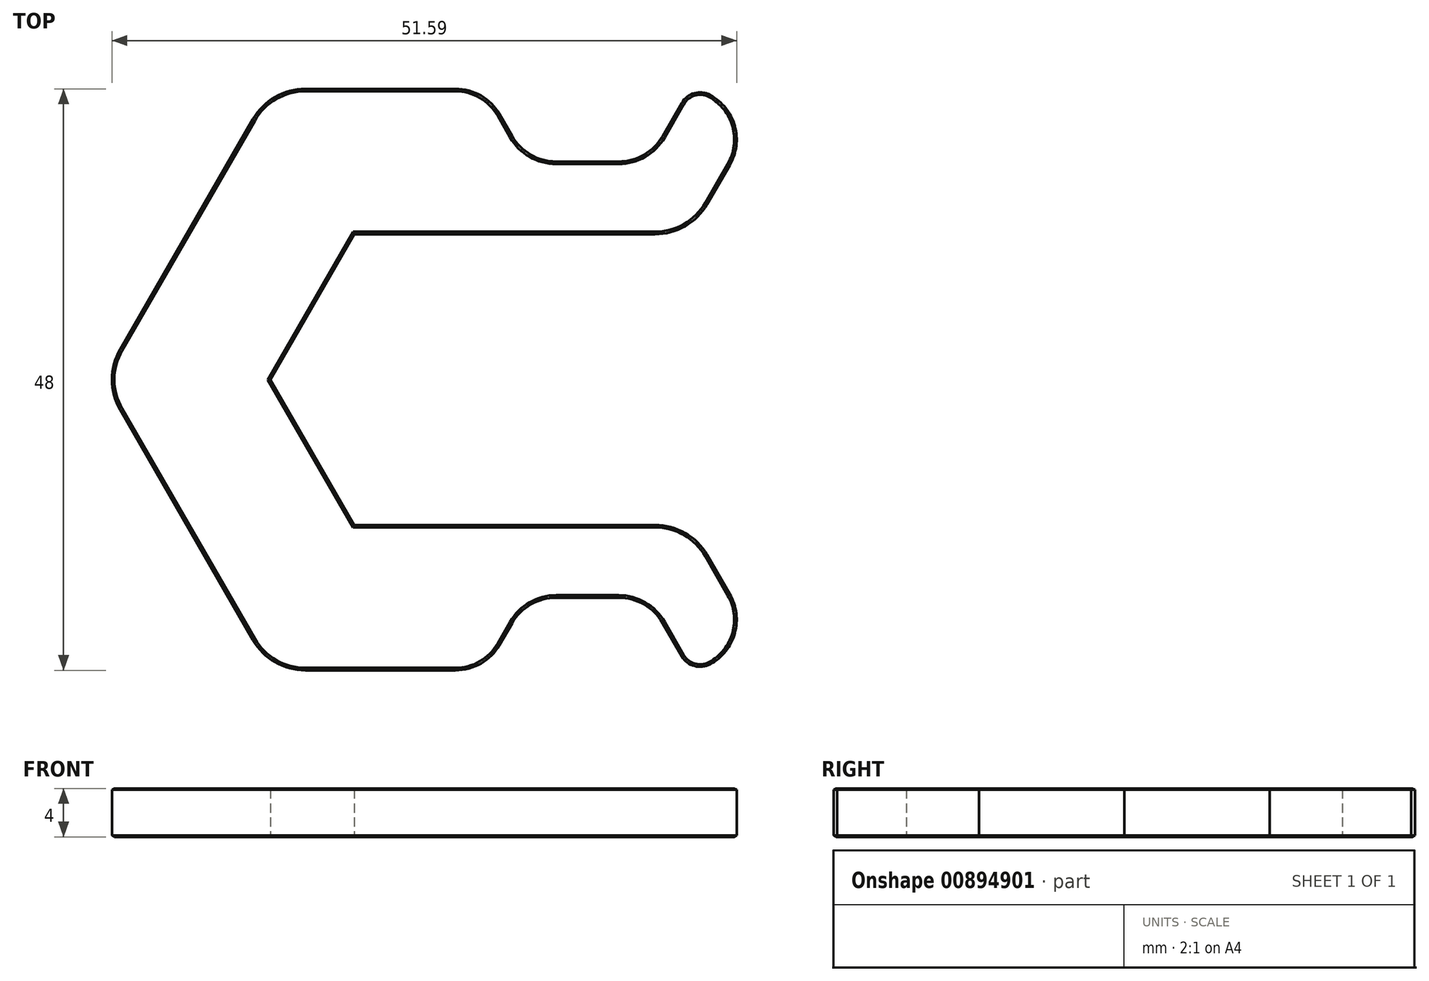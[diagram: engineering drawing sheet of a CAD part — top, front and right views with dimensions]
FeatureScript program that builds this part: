
annotation { "Feature Type Name" : "Feature", "Feature Type Description" : "" }
export const myFeature = defineFeature(function(context is Context, id is Id, definition is map)
    precondition{}
    {
        {
            var Q0;
            Q0=qCreatedBy(makeId("Top.planeOp"),FACE);
            var sketch = newSketch(context, id + "F0", { "sketchPlane" : qUnion([Q0])});
            skCircle(sketch, "E0.cCircle", {"center": v(0, 0) * mm, "radius": 12 * mm, "construction": true});
            skLineSegment(sketch, "E0.0", {"start": v(6.93, -12) * mm, "end": v(-6.93, -12) * mm});
            skLineSegment(sketch, "E0.1", {"start": v(-6.93, -12) * mm, "end": v(-13.86, 0) * mm});
            skLineSegment(sketch, "E0.2", {"start": v(-13.86, 0) * mm, "end": v(-6.93, 12) * mm});
            skLineSegment(sketch, "E0.3", {"start": v(-6.93, 12) * mm, "end": v(6.93, 12) * mm});
            skLineSegment(sketch, "E0.4", {"start": v(6.93, 12) * mm, "end": v(13.86, 0) * mm, "construction": true});
            skLineSegment(sketch, "E0.5", {"start": v(13.86, 0) * mm, "end": v(6.93, -12) * mm, "construction": true});
            skPoint(sketch, "E0.0.midPoint", {"position": v(0, -12) * mm});
            skCircle(sketch, "E1.cCircle", {"center": v(0, 0) * mm, "radius": 24 * mm, "construction": true});
            skLineSegment(sketch, "E1.0", {"start": v(13.86, -24) * mm, "end": v(-13.86, -24) * mm});
            skLineSegment(sketch, "E1.1", {"start": v(-13.86, -24) * mm, "end": v(-27.71, 0) * mm});
            skLineSegment(sketch, "E1.2", {"start": v(-27.71, 0) * mm, "end": v(-13.86, 24) * mm});
            skLineSegment(sketch, "E1.3", {"start": v(-13.86, 24) * mm, "end": v(13.86, 24) * mm});
            skLineSegment(sketch, "E1.4", {"start": v(13.86, 24) * mm, "end": v(27.71, 0) * mm});
            skLineSegment(sketch, "E1.5", {"start": v(27.71, 0) * mm, "end": v(13.86, -24) * mm});
            skPoint(sketch, "E1.0.midPoint", {"position": v(0, -24) * mm});
            skLineSegment(sketch, "E2", {"start": v(6.93, 12) * mm, "end": v(13.86, 24) * mm});
            skLineSegment(sketch, "E3", {"start": v(6.93, -12) * mm, "end": v(20.78, -12) * mm});
            skLineSegment(sketch, "E4", {"start": v(20.78, -12) * mm, "end": v(27.71, -24) * mm});
            skLineSegment(sketch, "E5", {"start": v(27.71, -24) * mm, "end": v(13.86, -24) * mm});
            skLineSegment(sketch, "E6", {"start": v(20.78, -24) * mm, "end": v(17.32, -18) * mm});
            skLineSegment(sketch, "E7", {"start": v(7.32, -18) * mm, "end": v(3.86, -24) * mm});
            skLineSegment(sketch, "E8", {"start": v(17.32, -18) * mm, "end": v(7.32, -18) * mm});
            skLineSegment(sketch, "E9", {"start": v(-13.86, 0) * mm, "end": v(-27.71, 0) * mm});
            skSolve(sketch);
        }
        {
            var Q0;
            Q0=makeQuery(id+"F0.imprint","IMPRINT",FACE,{"disambiguationData":[TD([[makeQuery(id+"F0.imprint","IMPRINT",EDGE,{"derivedFrom":sQuery(id+"F0.wireOp",EDGE,"E0.0")}),1.0]])]});
            var Q1;
            {var subQ2=sQuery(id+"F0.wireOp",EDGE,"E4");Q1=makeQuery(id+"F0.imprint","IMPRINT",FACE,{"disambiguationData":[TD([[makeQuery(id+"F0.imprint","IMPRINT",EDGE,{"derivedFrom":subQ2}),-1.0]])]});}
            extrude(context, id + "F1", {"entities" : qUnion([Q0, Q1]), "depth" : 4 * mm, "offsetDistance" : 25 * mm});
        }
        {
            var Q0;
            Q0=makeQuery(id+"F1.opExtrude","SWEPT_EDGE",EDGE,{"disambiguationData":[OSD([sQuery(id+"F0.wireOp",EDGE,"E1.0"),sQuery(id+"F0.wireOp",EDGE,"E1.1")])]});
            var Q1;
            Q1=makeQuery(id+"F1.opExtrude","SWEPT_EDGE",EDGE,{"disambiguationData":[OSD([sQuery(id+"F0.wireOp",EDGE,"E1.3"),sQuery(id+"F0.wireOp",EDGE,"E1.4"),sQuery(id+"F0.wireOp",EDGE,"E2")])]});
            var Q2;
            Q2=makeQuery(id+"F1.opExtrude","SWEPT_EDGE",EDGE,{"disambiguationData":[OSD([sQuery(id+"F0.wireOp",EDGE,"E1.5"),sQuery(id+"F0.wireOp",EDGE,"E3")])]});
            fillet(context, id + "F2", {"entities" : qUnion([Q0, Q1, Q2]), "radius" : 5 * mm, "tangentPropagation" : true, "allowEdgeOverflow" : false});
        }
        {
            var Q0;
            Q0=makeQuery(id+"F1.opExtrude","SWEPT_EDGE",EDGE,{"disambiguationData":[OSD([sQuery(id+"F0.wireOp",EDGE,"E1.0"),sQuery(id+"F0.wireOp",EDGE,"E7")])]});
            var Q1;
            Q1=makeQuery(id+"F1.opExtrude","SWEPT_EDGE",EDGE,{"disambiguationData":[OSD([sQuery(id+"F0.wireOp",EDGE,"E7"),sQuery(id+"F0.wireOp",EDGE,"E8")])]});
            var Q2;
            Q2=makeQuery(id+"F1.opExtrude","SWEPT_EDGE",EDGE,{"disambiguationData":[OSD([sQuery(id+"F0.wireOp",EDGE,"E1.5"),sQuery(id+"F0.wireOp",EDGE,"E6"),sQuery(id+"F0.wireOp",EDGE,"E8")])]});
            var Q3;
            Q3=makeQuery(id+"F1.opExtrude","SWEPT_EDGE",EDGE,{"disambiguationData":[OSD([sQuery(id+"F0.wireOp",EDGE,"E4"),sQuery(id+"F0.wireOp",EDGE,"E5")])]});
            fillet(context, id + "F3", {"entities" : qUnion([Q0, Q1, Q2, Q3]), "radius" : 4.2 * mm, "tangentPropagation" : true, "allowEdgeOverflow" : false});
        }
        {
            var Q0;
            Q0=makeQuery(id+"F3.opFillet","BLEND_EDGE",EDGE,{"blendedFrom":[makeQuery(id+"F1.opExtrude","SWEPT_EDGE",EDGE,{"disambiguationData":[OSD([sQuery(id+"F0.wireOp",EDGE,"E4"),sQuery(id+"F0.wireOp",EDGE,"E5")])]}),makeQuery(id+"F1.opExtrude","SWEPT_FACE",FACE,{"disambiguationData":[OSD([sQuery(id+"F0.wireOp",EDGE,"E6")])]})],"blendedInto":[makeQuery(id+"F1.opExtrude","SWEPT_FACE",FACE,{"disambiguationData":[OSD([sQuery(id+"F0.wireOp",EDGE,"E6")])]})]});
            fillet(context, id + "F4", {"entities" : qUnion([Q0]), "radius" : 1.75 * mm, "tangentPropagation" : true, "allowEdgeOverflow" : false});
        }
        {
            var Q0;
            Q0=makeQuery(id+"F1.opExtrude","SWEPT_BODY",BODY,{"disambiguationData":[OSD([sQuery(id+"F0.wireOp",EDGE,"E0.0"),sQuery(id+"F0.wireOp",EDGE,"E0.1"),sQuery(id+"F0.wireOp",EDGE,"E1.0"),sQuery(id+"F0.wireOp",EDGE,"E1.1"),sQuery(id+"F0.wireOp",EDGE,"E3"),sQuery(id+"F0.wireOp",EDGE,"E4"),sQuery(id+"F0.wireOp",EDGE,"E5"),sQuery(id+"F0.wireOp",EDGE,"E6"),sQuery(id+"F0.wireOp",EDGE,"E7"),sQuery(id+"F0.wireOp",EDGE,"E8"),sQuery(id+"F0.wireOp",EDGE,"E9")])]});
            var Q1;
            Q1=makeQuery(id+"F1.opExtrude","SWEPT_FACE",FACE,{"disambiguationData":[OSD([sQuery(id+"F0.wireOp",EDGE,"E9")])]});
            mirror(context, id + "F5", {"operationType" : NewBodyOperationType.ADD, "entities" : qUnion([Q0]), "mirrorPlane" : qUnion([Q1])});
        }
        {
            var Q0;
            {var subQ0=makeQuery(id+"F1.opExtrude","SWEPT_EDGE",EDGE,{"disambiguationData":[OSD([sQuery(id+"F0.wireOp",EDGE,"E1.1"),sQuery(id+"F0.wireOp",EDGE,"E1.2"),sQuery(id+"F0.wireOp",EDGE,"E9")])]});Q0=makeQuery(id+"F5.boolean.opBoolean","MERGE",EDGE,{"derivedFrom":[subQ0,makeQuery(id+"F5.opPattern","COPY",EDGE,{"derivedFrom":subQ0,"instanceName":"1"})]});}
            fillet(context, id + "F6", {"entities" : qUnion([Q0]), "radius" : 5 * mm, "tangentPropagation" : true, "allowEdgeOverflow" : false});
        }
        {
            var Q0;
            {var subQ0=makeQuery(id+"F1.opExtrude","CAP_FACE",FACE,{"disambiguationData":[OSD([sQuery(id+"F0.wireOp",EDGE,"E0.0"),sQuery(id+"F0.wireOp",EDGE,"E0.1"),sQuery(id+"F0.wireOp",EDGE,"E1.0"),sQuery(id+"F0.wireOp",EDGE,"E1.1"),sQuery(id+"F0.wireOp",EDGE,"E3"),sQuery(id+"F0.wireOp",EDGE,"E4"),sQuery(id+"F0.wireOp",EDGE,"E5"),sQuery(id+"F0.wireOp",EDGE,"E6"),sQuery(id+"F0.wireOp",EDGE,"E7"),sQuery(id+"F0.wireOp",EDGE,"E8"),sQuery(id+"F0.wireOp",EDGE,"E9")])],"isStart":false});Q0=makeQuery(id+"F5.boolean.opBoolean","MERGE",FACE,{"derivedFrom":[subQ0,makeQuery(id+"F5.opPattern","COPY",FACE,{"derivedFrom":subQ0,"instanceName":"1"})]});}
            var Q1;
            Q1=makeQuery(id+"F1.opExtrude","CAP_EDGE",EDGE,{"disambiguationData":[OSD([sQuery(id+"F0.wireOp",EDGE,"E1.0")])],"isStart":true});
            var Q2;
            Q2=makeQuery(id+"F1.opExtrude","CAP_EDGE",EDGE,{"disambiguationData":[OSD([sQuery(id+"F0.wireOp",EDGE,"E0.1")])],"isStart":true});
            var Q3;
            Q3=makeQuery(id+"F5.opPattern","COPY",EDGE,{"derivedFrom":makeQuery(id+"F1.opExtrude","CAP_EDGE",EDGE,{"disambiguationData":[OSD([sQuery(id+"F0.wireOp",EDGE,"E0.1")])],"isStart":true}),"instanceName":"1"});
            chamfer(context, id + "F7", {"entities" : qUnion([Q0, Q1, Q2, Q3]), "chamferType" : ChamferType.TWO_OFFSETS, "width1" : 0.2 * mm, "oppositeDirection" : false, "width2" : 0.1 * mm, "tangentPropagation" : true});
        }
    });
